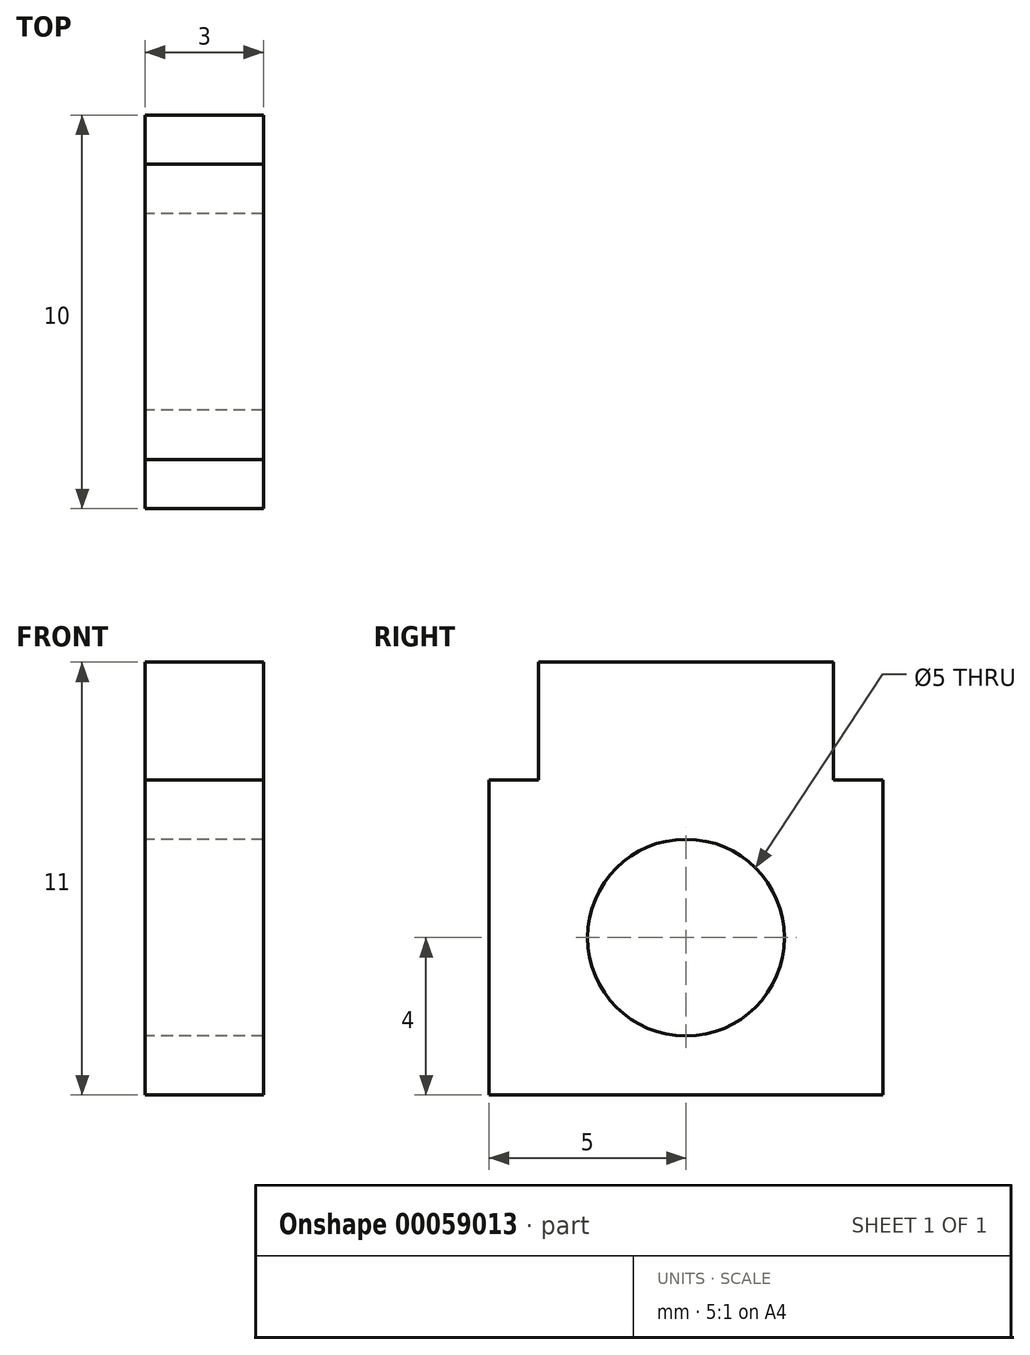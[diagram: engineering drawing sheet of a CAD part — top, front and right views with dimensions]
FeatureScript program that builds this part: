
annotation { "Feature Type Name" : "Feature", "Feature Type Description" : "" }
export const myFeature = defineFeature(function(context is Context, id is Id, definition is map)
    precondition{}
    {
        {
            var Q0;
            Q0=qCreatedBy(makeId("Right.planeOp"),FACE);
            var sketch = newSketch(context, id + "F0", { "sketchPlane" : qUnion([Q0])});
            skLineSegment(sketch, "E0.rect.top", {"start": v(-5, -4) * mm, "end": v(5, -4) * mm});
            skLineSegment(sketch, "E0.rect.left", {"start": v(-5, 4) * mm, "end": v(-5, -4) * mm});
            skLineSegment(sketch, "E0.rect.right", {"start": v(5, 4) * mm, "end": v(5, -4) * mm});
            skPoint(sketch, "E0.rect.middle", {"position": v(0, 0) * mm});
            skCircle(sketch, "E1", {"center": v(0, 0) * mm, "radius": 2.5 * mm});
            skLineSegment(sketch, "E2", {"start": v(-5, 4) * mm, "end": v(-3.75, 4) * mm});
            skLineSegment(sketch, "E3.top", {"start": v(-3.75, 7) * mm, "end": v(3.75, 7) * mm});
            skLineSegment(sketch, "E3.left", {"start": v(-3.75, 4) * mm, "end": v(-3.75, 7) * mm});
            skLineSegment(sketch, "E3.right", {"start": v(3.75, 4) * mm, "end": v(3.75, 7) * mm});
            skLineSegment(sketch, "E4.trimOffspring", {"start": v(3.75, 4) * mm, "end": v(5, 4) * mm});
            skSolve(sketch);
        }
        {
            var Q0;
            Q0 = qSketchRegion(id + "F0", true);
            extrude(context, id + "F1", {"entities" : qUnion([Q0]), "depth" : 3 * mm});
        }
    });
